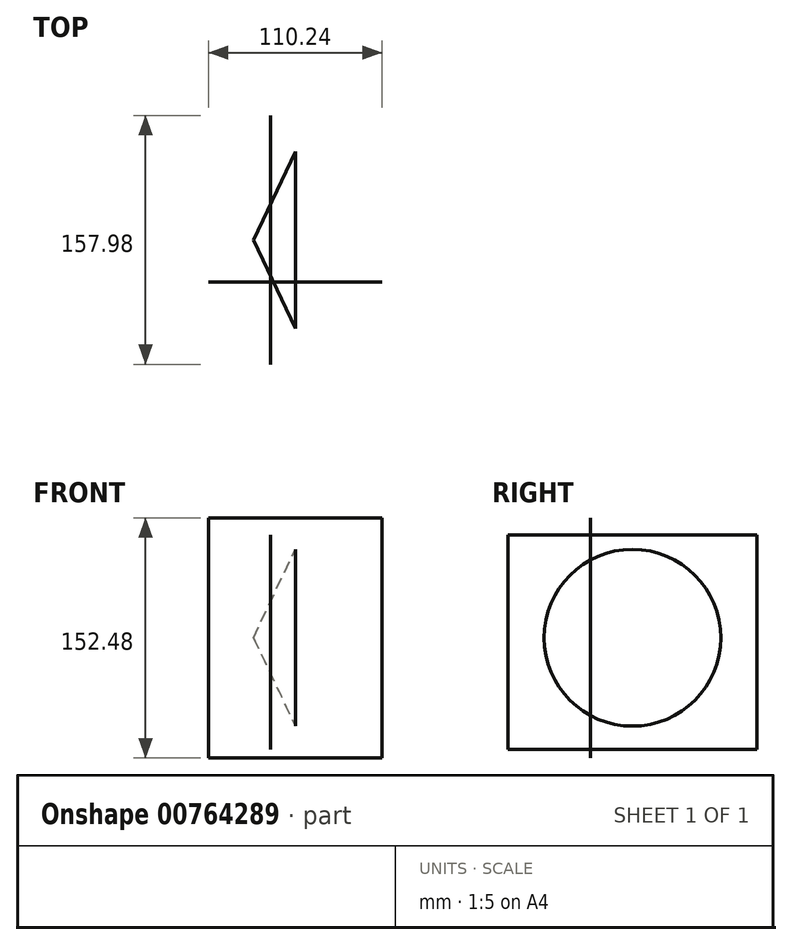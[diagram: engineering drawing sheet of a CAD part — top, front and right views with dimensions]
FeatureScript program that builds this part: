
annotation { "Feature Type Name" : "Feature", "Feature Type Description" : "" }
export const myFeature = defineFeature(function(context is Context, id is Id, definition is map)
    precondition{}
    {
        {
            var Q0;
            Q0=qCreatedBy(makeId("Front.planeOp"),FACE);
            var sketch = newSketch(context, id + "F0", { "sketchPlane" : qUnion([Q0])});
            skLineSegment(sketch, "E0", {"start": v(0, 56.14) * mm, "end": v(-26.64, 0) * mm});
            skLineSegment(sketch, "E1", {"start": v(-26.64, 0) * mm, "end": v(0, 0) * mm});
            skLineSegment(sketch, "E2", {"start": v(0, 0) * mm, "end": v(0, 56.14) * mm});
            skSolve(sketch);
        }
        {
            var Q0;
            Q0=sQuery(id+"F0.wireOp",EDGE,"E0");
            var Q1;
            Q1=sQuery(id+"F0.wireOp",EDGE,"E1");
            revolve(context, id + "F1", {"bodyType" : ToolBodyType.SURFACE, "surfaceOperationType" : NewSurfaceOperationType.NEW, "surfaceEntities" : qUnion([Q0]), "axis" : qUnion([Q1]), "revolveType" : RevolveType.FULL});
        }
        {
            var Q0;
            Q0=qCreatedBy(makeId("Right.planeOp"),FACE);
            var sketch = newSketch(context, id + "F2", { "sketchPlane" : qUnion([Q0])});
            skLineSegment(sketch, "E3", {"start": v(-26.6, 76.17) * mm, "end": v(-26.6, -76.31) * mm});
            skSolve(sketch);
        }
        {
            var Q0;
            Q0=sQuery(id+"F2.wireOp",EDGE,"E3");
            extrude(context, id + "F3", {"bodyType" : ToolBodyType.SURFACE, "surfaceEntities" : qUnion([Q0]), "endBound" : BoundingType.SYMMETRIC, "oppositeDirection" : true, "depth" : 110.24 * mm, "offsetDistance" : 25.4 * mm});
        }
        {
            var Q0;
            Q0=qCreatedBy(makeId("Front.planeOp"),FACE);
            var sketch = newSketch(context, id + "F4", { "sketchPlane" : qUnion([Q0])});
            skLineSegment(sketch, "E4", {"start": v(-15.77, 65.16) * mm, "end": v(-15.77, -70.8) * mm});
            skSolve(sketch);
        }
        {
            var Q0;
            Q0=sQuery(id+"F4.wireOp",EDGE,"E4");
            extrude(context, id + "F5", {"bodyType" : ToolBodyType.SURFACE, "surfaceEntities" : qUnion([Q0]), "endBound" : BoundingType.SYMMETRIC, "depth" : 158 * mm, "offsetDistance" : 25.4 * mm});
        }
    });
